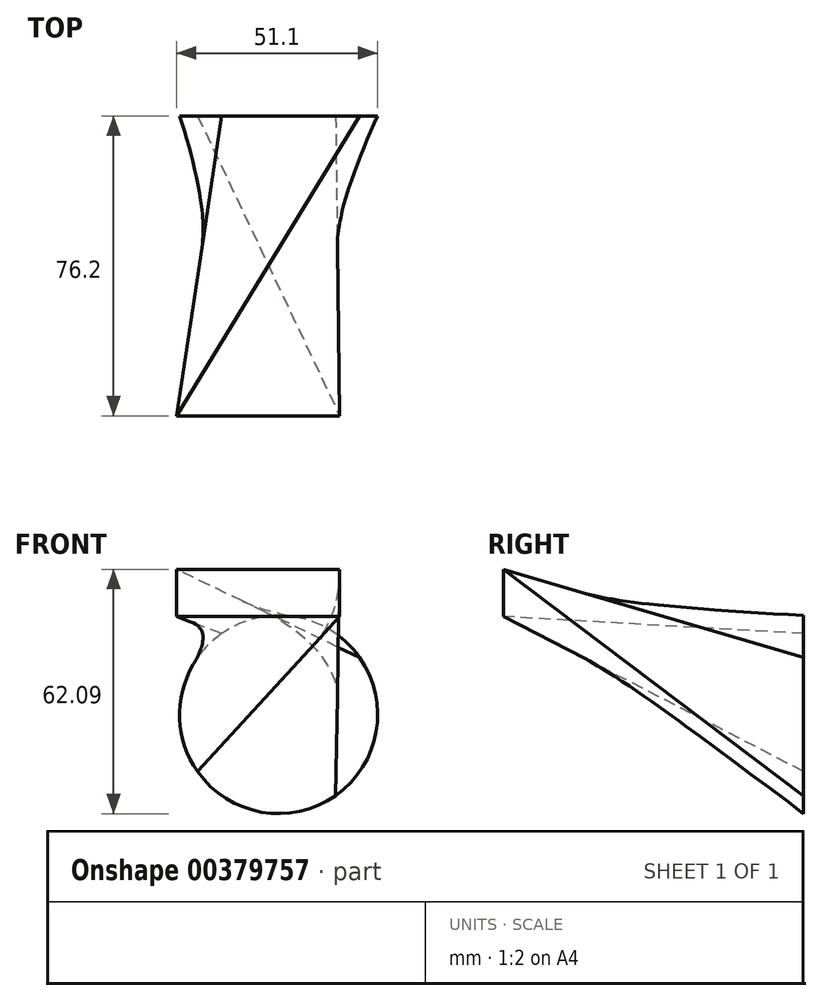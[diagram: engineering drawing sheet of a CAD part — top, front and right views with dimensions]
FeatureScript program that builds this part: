
annotation { "Feature Type Name" : "Feature", "Feature Type Description" : "" }
export const myFeature = defineFeature(function(context is Context, id is Id, definition is map)
    precondition{}
    {
        {
            var Q0;
            Q0=qCreatedBy(makeId("Front.planeOp"),FACE);
            var sketch = newSketch(context, id + "F0", { "sketchPlane" : qUnion([Q0])});
            skCircle(sketch, "E0", {"center": v(-8.25, 6.63) * mm, "radius": 25.16 * mm});
            skSolve(sketch);
        }
        {
            var Q0;
            Q0=qCreatedBy(makeId("Front.planeOp"),FACE);
            cPlane(context, id + "F1", {"entities" : qUnion([Q0]), "cplaneType" : CPlaneType.OFFSET, "offset" : 76.2 * mm, "width" : 152.4 * mm, "height" : 152.4 * mm});
        }
        {
            var Q0;
            Q0=qCreatedBy(id+"F1.planeOp",FACE);
            var sketch = newSketch(context, id + "F2", { "sketchPlane" : qUnion([Q0])});
            skLineSegment(sketch, "E1.bottom", {"start": v(-34.19, 43.55) * mm, "end": v(7.22, 43.55) * mm});
            skLineSegment(sketch, "E1.top", {"start": v(-34.19, 31.52) * mm, "end": v(7.22, 31.52) * mm});
            skLineSegment(sketch, "E1.left", {"start": v(-34.19, 43.55) * mm, "end": v(-34.19, 31.52) * mm});
            skLineSegment(sketch, "E1.right", {"start": v(7.22, 43.55) * mm, "end": v(7.22, 31.52) * mm});
            skSolve(sketch);
        }
        {
            var Q0;
            Q0=makeQuery(id+"F0.imprint","IMPRINT",FACE,{"disambiguationData":[TD([[makeQuery(id+"F0.imprint","IMPRINT",EDGE,{"derivedFrom":sQuery(id+"F0.wireOp",EDGE,"E0")}),1.0]])]});
            var Q1;
            Q1=makeQuery(id+"F2.imprint","IMPRINT",FACE,{"disambiguationData":[TD([[makeQuery(id+"F2.imprint","IMPRINT",EDGE,{"derivedFrom":sQuery(id+"F2.wireOp",EDGE,"E1.bottom")}),-1.0]])]});
            loft(context, id + "F3", {"sheetProfilesArray" : [{ "sheetProfileEntities" : qUnion([Q0]) }, { "sheetProfileEntities" : qUnion([Q1]) }]});
        }
    });
